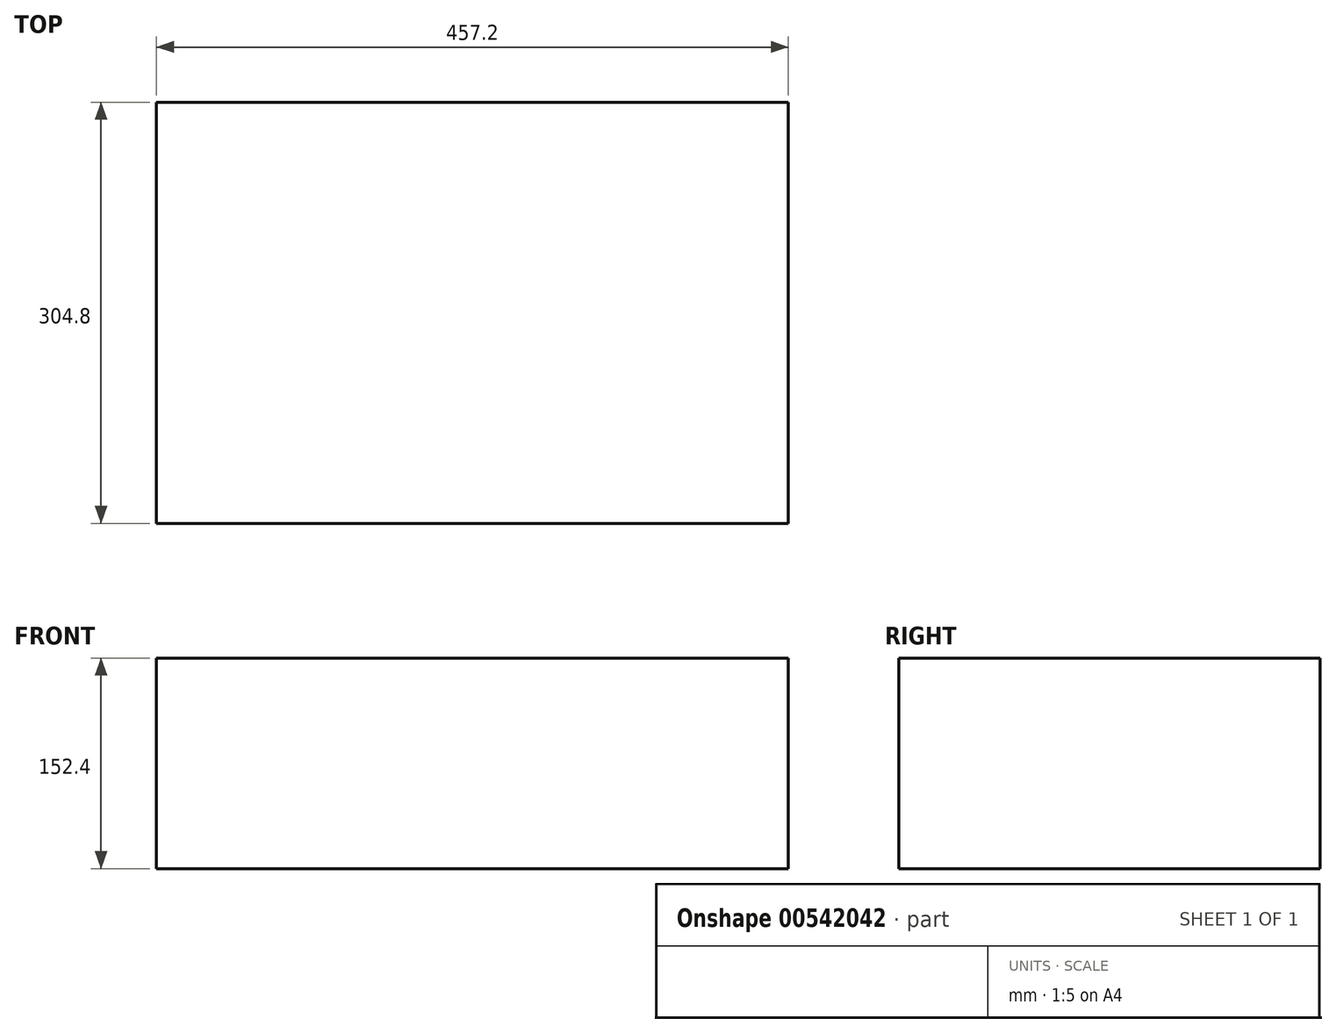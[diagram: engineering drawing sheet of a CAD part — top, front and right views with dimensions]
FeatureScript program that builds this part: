
annotation { "Feature Type Name" : "Feature", "Feature Type Description" : "" }
export const myFeature = defineFeature(function(context is Context, id is Id, definition is map)
    precondition{}
    {
        {
            var Q0;
            Q0=qCreatedBy(makeId("Front.planeOp"),FACE);
            var sketch = newSketch(context, id + "F0", { "sketchPlane" : qUnion([Q0])});
            skLineSegment(sketch, "E0.bottom", {"start": v(-228.6, 60.96) * mm, "end": v(228.6, 60.96) * mm});
            skLineSegment(sketch, "E0.top", {"start": v(-228.6, -91.44) * mm, "end": v(228.6, -91.44) * mm});
            skLineSegment(sketch, "E0.left", {"start": v(-228.6, 60.96) * mm, "end": v(-228.6, -91.44) * mm});
            skLineSegment(sketch, "E0.right", {"start": v(228.6, 60.96) * mm, "end": v(228.6, -91.44) * mm});
            skPoint(sketch, "E0.middle", {"position": v(0, -15.24) * mm});
            skSolve(sketch);
        }
        {
            var Q0;
            Q0=makeQuery(id+"F0.imprint","IMPRINT",FACE,{"disambiguationData":[TD([[makeQuery(id+"F0.imprint","IMPRINT",EDGE,{"derivedFrom":sQuery(id+"F0.wireOp",EDGE,"E0.bottom")}),-1.0]])]});
            extrude(context, id + "F1", {"entities" : qUnion([Q0]), "depth" : 304.8 * mm, "offsetDistance" : 25.4 * mm});
        }
    });
